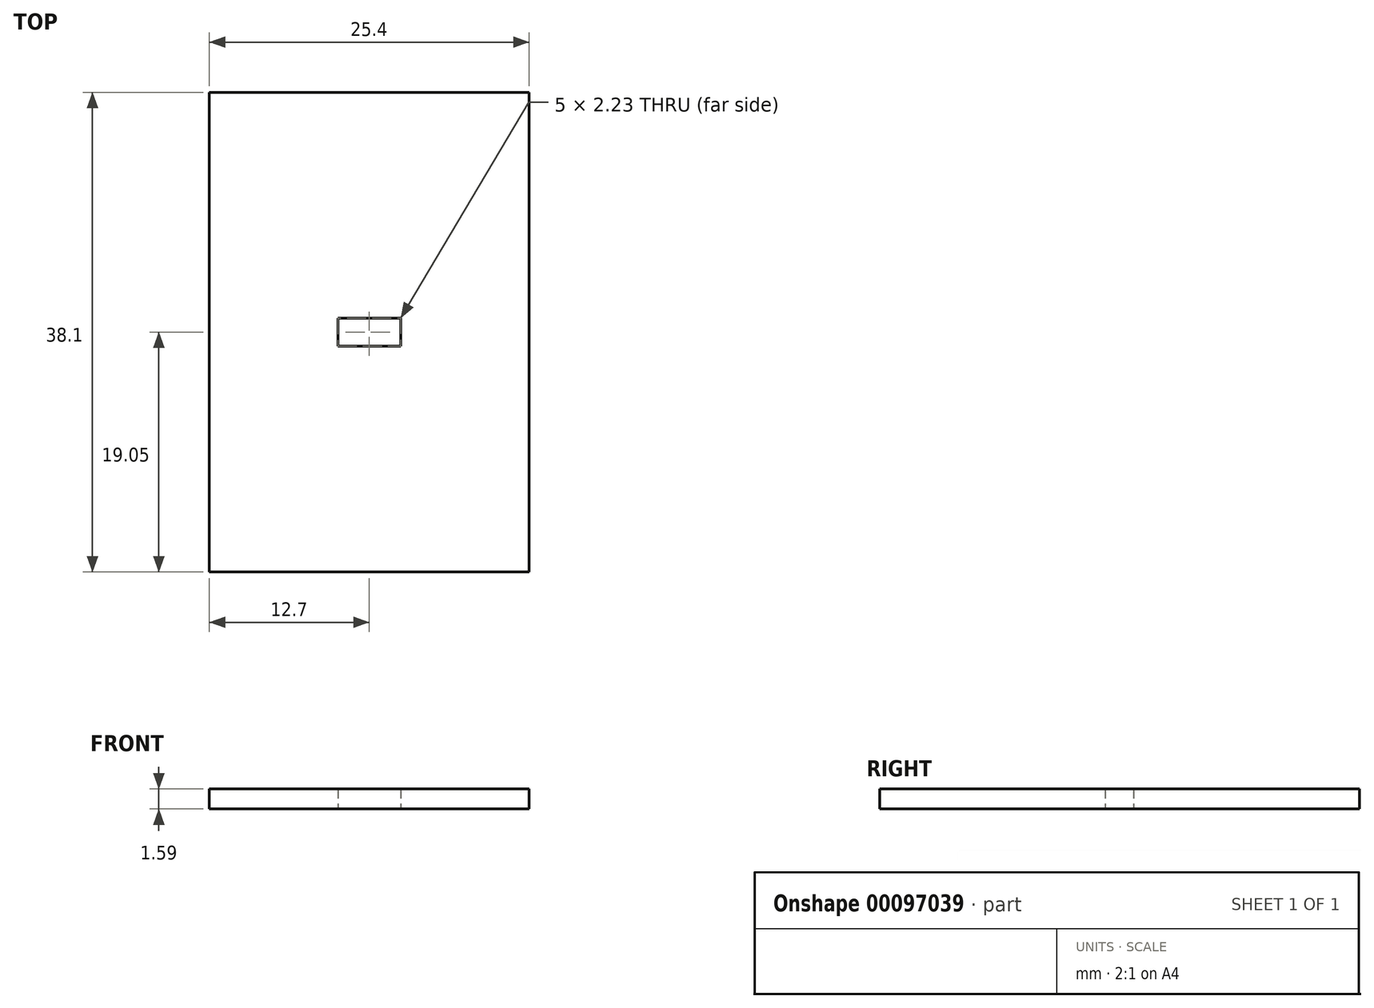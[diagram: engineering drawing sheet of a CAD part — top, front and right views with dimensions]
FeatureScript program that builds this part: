
annotation { "Feature Type Name" : "Feature", "Feature Type Description" : "" }
export const myFeature = defineFeature(function(context is Context, id is Id, definition is map)
    precondition{}
    {
        {
            var Q0;
            Q0=qCreatedBy(makeId("Top.planeOp"),FACE);
            var sketch = newSketch(context, id + "F0", { "sketchPlane" : qUnion([Q0])});
            skLineSegment(sketch, "E0.bottom", {"start": v(12.7, 19.05) * mm, "end": v(-12.7, 19.05) * mm});
            skLineSegment(sketch, "E0.top", {"start": v(12.7, -19.05) * mm, "end": v(-12.7, -19.05) * mm});
            skLineSegment(sketch, "E0.left", {"start": v(12.7, 19.05) * mm, "end": v(12.7, -19.05) * mm});
            skLineSegment(sketch, "E0.right", {"start": v(-12.7, 19.05) * mm, "end": v(-12.7, -19.05) * mm});
            skPoint(sketch, "E0.middle", {"position": v(0, 0) * mm});
            skLineSegment(sketch, "E1.bottom", {"start": v(2.5, 2.5) * mm, "end": v(-2.5, 2.5) * mm, "construction": true});
            skLineSegment(sketch, "E1.top", {"start": v(2.5, -2.5) * mm, "end": v(-2.5, -2.5) * mm, "construction": true});
            skLineSegment(sketch, "E1.left", {"start": v(2.5, 2.5) * mm, "end": v(2.5, -2.5) * mm, "construction": true});
            skLineSegment(sketch, "E1.right", {"start": v(-2.5, 2.5) * mm, "end": v(-2.5, -2.5) * mm, "construction": true});
            skLineSegment(sketch, "E2.bottom", {"start": v(2.5, 1.11) * mm, "end": v(-2.5, 1.11) * mm});
            skLineSegment(sketch, "E2.top", {"start": v(2.5, -1.11) * mm, "end": v(-2.5, -1.11) * mm});
            skLineSegment(sketch, "E2.left", {"start": v(2.5, 1.11) * mm, "end": v(2.5, -1.11) * mm});
            skLineSegment(sketch, "E2.right", {"start": v(-2.5, 1.11) * mm, "end": v(-2.5, -1.11) * mm});
            skSolve(sketch);
        }
        {
            var Q0;
            Q0=makeQuery(id+"F0.imprint","IMPRINT",FACE,{"disambiguationData":[TD([[makeQuery(id+"F0.imprint","IMPRINT",EDGE,{"derivedFrom":sQuery(id+"F0.wireOp",EDGE,"E0.bottom")}),1.0]])]});
            extrude(context, id + "F1", {"entities" : qUnion([Q0]), "depth" : 1.59 * mm});
        }
    });
